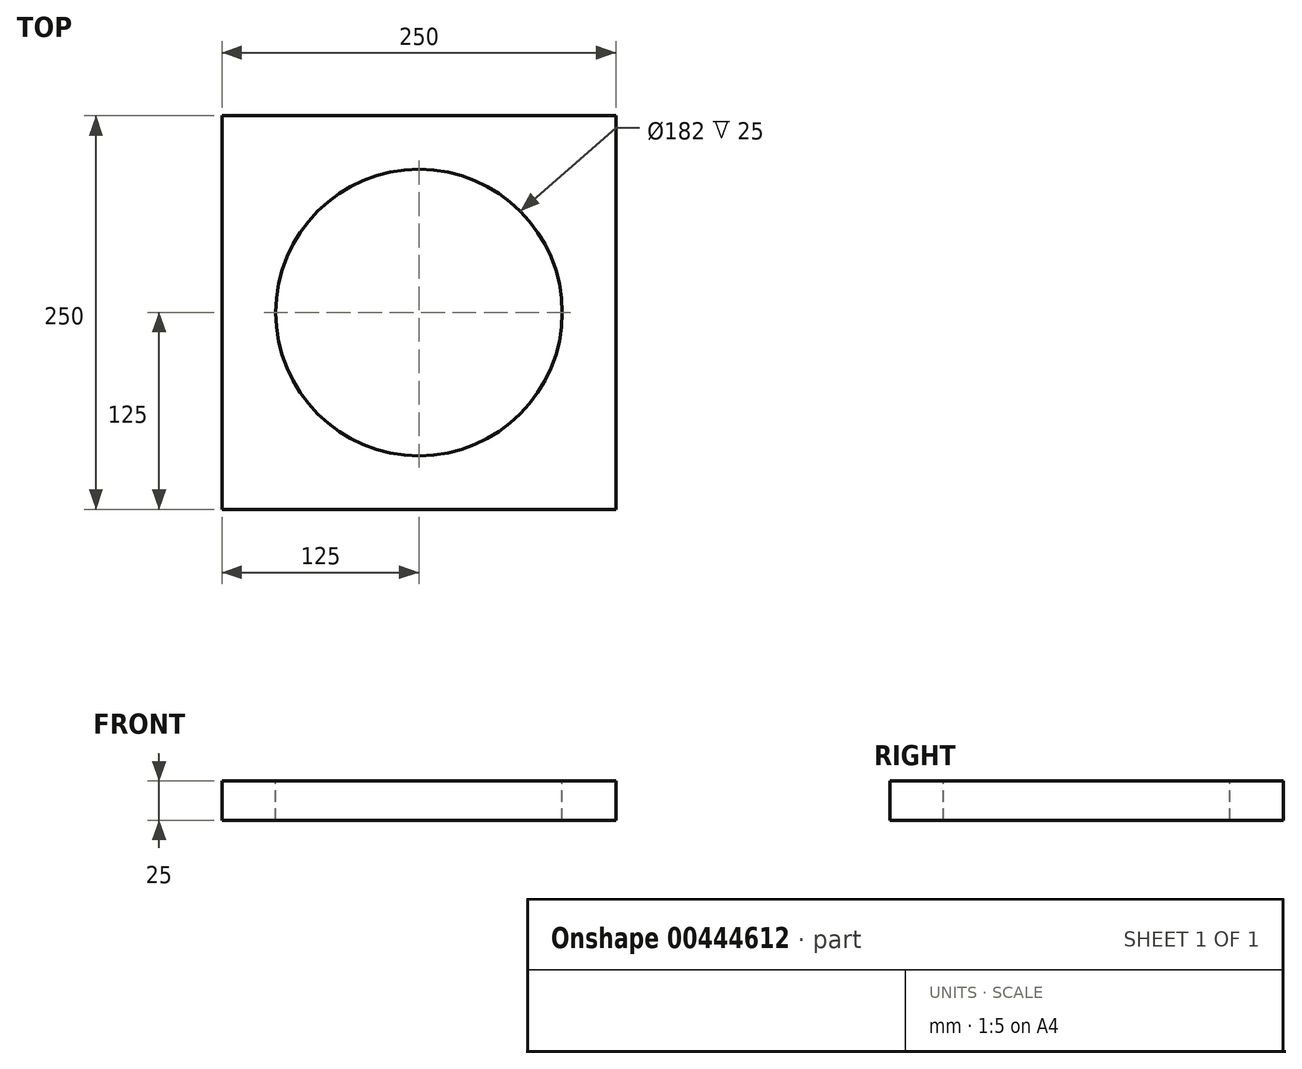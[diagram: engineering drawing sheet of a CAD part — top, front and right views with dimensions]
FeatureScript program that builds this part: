
annotation { "Feature Type Name" : "Feature", "Feature Type Description" : "" }
export const myFeature = defineFeature(function(context is Context, id is Id, definition is map)
    precondition{}
    {
        {
            var Q0;
            Q0=qCreatedBy(makeId("Top.planeOp"),FACE);
            var sketch = newSketch(context, id + "F0", { "sketchPlane" : qUnion([Q0])});
            skCircle(sketch, "E0", {"center": v(0, 0) * mm, "radius": 91 * mm});
            skLineSegment(sketch, "E1.bottom", {"start": v(125, -125) * mm, "end": v(-125, -125) * mm});
            skLineSegment(sketch, "E1.top", {"start": v(125, 125) * mm, "end": v(-125, 125) * mm});
            skLineSegment(sketch, "E1.left", {"start": v(125, -125) * mm, "end": v(125, 125) * mm});
            skLineSegment(sketch, "E1.right", {"start": v(-125, -125) * mm, "end": v(-125, 125) * mm});
            skSolve(sketch);
        }
        {
            var Q0;
            Q0=makeQuery(id+"F0.imprint","IMPRINT",FACE,{"disambiguationData":[TD([[makeQuery(id+"F0.imprint","IMPRINT",EDGE,{"derivedFrom":sQuery(id+"F0.wireOp",EDGE,"E0")}),-1.0]])]});
            extrude(context, id + "F1", {"entities" : qUnion([Q0]), "oppositeDirection" : true, "depth" : 25 * mm});
        }
    });
